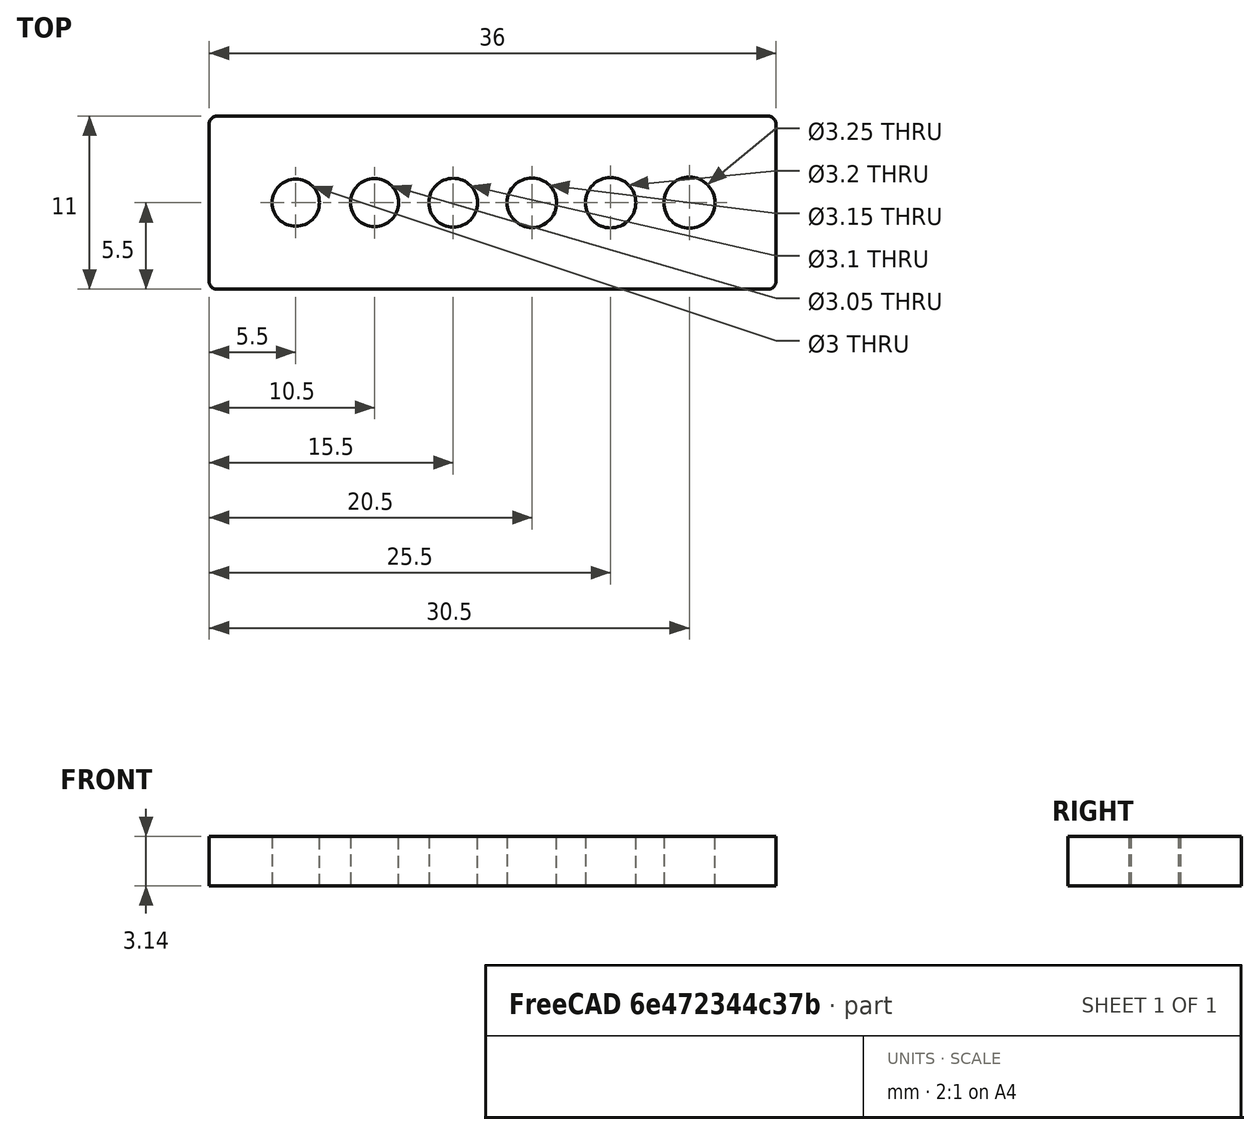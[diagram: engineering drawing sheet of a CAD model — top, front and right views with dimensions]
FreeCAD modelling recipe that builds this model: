
FCSTD DOCUMENT  (FreeCAD 1.0R39285 (Git))
Label: Hole-Tests_v2
License: Creative Commons Attribution 4.0
objects: Sketcher::SketchObject×1, PartDesign::Pad×1, PartDesign::Body×1
note: 6 computed .brp shape members not serialized (recipe doc carries the construction recipe); baked Part::Feature solids carry a one-line shape summary decoded from their .brp

FEATURE [Sketcher::SketchObject] Sketch
  ArcFitTolerance = 1e-06
  AttachmentSupport = -> [XY_Plane]
  FullyConstrained = true
  MakeInternals = false
  MapMode = 5
  sketch-geometry (16):
    g0: LineSegment StartX=-18 StartY=5 StartZ=0 EndX=-18 EndY=-5 EndZ=0
    g1: LineSegment StartX=-17.5 StartY=-5.5 StartZ=0 EndX=17.5 EndY=-5.5 EndZ=0
    g2: LineSegment StartX=18 StartY=-5 StartZ=0 EndX=18 EndY=5 EndZ=0
    g3: LineSegment StartX=17.5 StartY=5.5 StartZ=0 EndX=-17.5 EndY=5.5 EndZ=0
    g4: ArcOfCircle CenterX=-17.5 CenterY=5 CenterZ=0 NormalX=0 NormalY=0 NormalZ=1 AngleXU=0 Radius=0.5 StartAngle=1.5708 EndAngle=3.14159
    g5: ArcOfCircle CenterX=-17.5 CenterY=-5 CenterZ=0 NormalX=0 NormalY=0 NormalZ=1 AngleXU=0 Radius=0.5 StartAngle=3.14159 EndAngle=4.71239
    g6: ArcOfCircle CenterX=17.5 CenterY=-5 CenterZ=0 NormalX=0 NormalY=0 NormalZ=1 AngleXU=0 Radius=0.5 StartAngle=4.71239 EndAngle=6.28319
    g7: ArcOfCircle CenterX=17.5 CenterY=5 CenterZ=0 NormalX=0 NormalY=0 NormalZ=1 AngleXU=0 Radius=0.5 StartAngle=4.2249e-12 EndAngle=1.5708
    g8: GeomPoint [constr] X=-18 Y=5.5 Z=0
    g9: GeomPoint [constr] X=18 Y=-5.5 Z=0
    g10: Circle CenterX=-12.5 CenterY=0 CenterZ=0 NormalX=0 NormalY=0 NormalZ=1 AngleXU=0 Radius=1.5
    g11: Circle CenterX=-7.5 CenterY=0 CenterZ=0 NormalX=0 NormalY=0 NormalZ=1 AngleXU=0 Radius=1.525
    g12: Circle CenterX=-2.5 CenterY=0 CenterZ=0 NormalX=0 NormalY=0 NormalZ=1 AngleXU=0 Radius=1.55
    g13: Circle CenterX=2.5 CenterY=0 CenterZ=0 NormalX=0 NormalY=0 NormalZ=1 AngleXU=0 Radius=1.4
    g14: Circle CenterX=7.5 CenterY=0 CenterZ=0 NormalX=0 NormalY=0 NormalZ=1 AngleXU=0 Radius=1.45
    g15: Circle CenterX=12.5 CenterY=2.004e-13 CenterZ=0 NormalX=0 NormalY=0 NormalZ=1 AngleXU=0 Radius=1.5
  constraints (39):
    c: Tangent(g0,g4) = -1.5708
    c: Tangent(g0,g5) = -1.5708
    c: Tangent(g1,g5) = -1.5708
    c: Tangent(g1,g6) = -1.5708
    c: Tangent(g2,g6) = -1.5708
    c: Tangent(g2,g7) = -1.5708
    c: Tangent(g3,g7) = -1.5708
    c: Tangent(g3,g4) = -1.5708
    c: Vertical(g0)
    c: Vertical(g2)
    c: Horizontal(g1)
    c: Horizontal(g3)
    c: Equal(g5,g6)
    c: PointOnObject(g8,g0)
    c: PointOnObject(g8,g3)
    c: PointOnObject(g9,g1)
    c: PointOnObject(g9,g2)
    c: Symmetric(g4,g7,g-2)
    c: Symmetric(g4,g5,g-1)
    c: PointOnObject(g15,g-1)
    c: PointOnObject(g14,g-1)
    c: PointOnObject(g13,g-1)
    c: PointOnObject(g11,g-1)
    c: PointOnObject(g10,g-1)
    c: Diameter(g10) = 3
    c: Diameter(g11) = 3.05
    c: Diameter(g12) = 3.1
    c: Diameter(g13) = 2.8
    c: Diameter(g14) = 2.9
    c: Diameter(g15) = 3
    c: DistanceX(g10,g11) = 5
    c: DistanceX(g11,g12) = 5
    c: DistanceX(g12,g13) = 5
    c: DistanceX(g13,g14) = 5
    c: DistanceX(g14,g15) = 5
    c: Symmetric(g12,g13,g-2)
    c: Diameter(g4) = 1
    c: DistanceX(g15,g7) = 5
    c: DistanceY(g15,g7) = 5
FEATURE [PartDesign::Pad] Pad
  Direction = (0,0,1)
  Length = 3.14
  Length2 = 10
  Profile = -> Sketch
  ReferenceAxis = -> Sketch [N_Axis]
  Refine = true
  Suppressed = false
  Type = 0
FEATURE [PartDesign::Body] Body
  AllowCompound = false
  Group = -> [Sketch,Pad]
  Origin = -> Origin
  Tip = -> Pad
